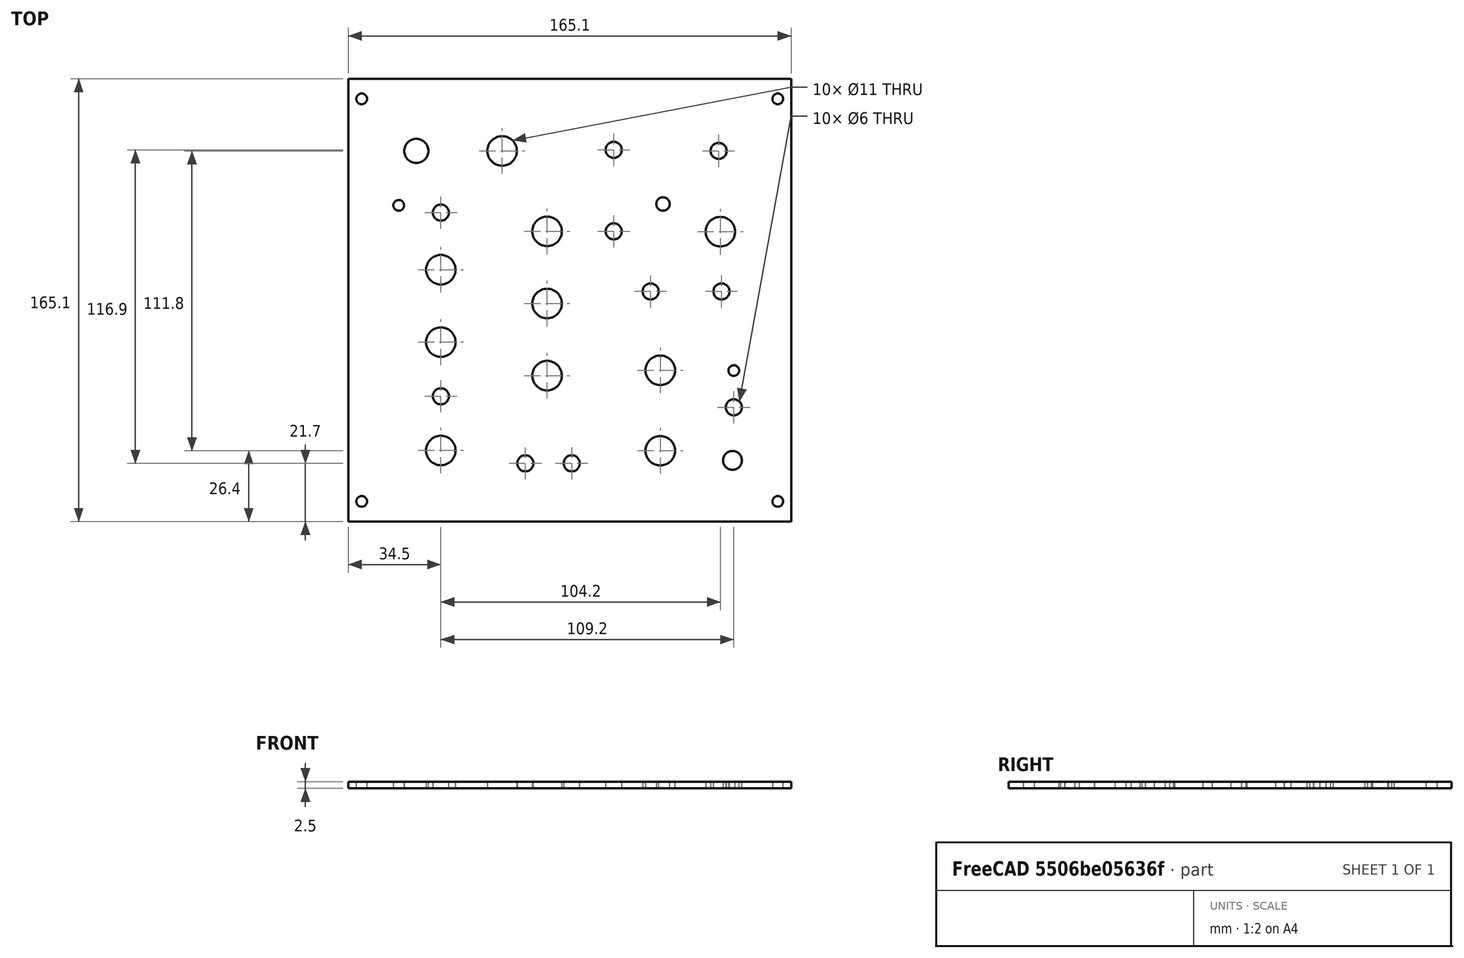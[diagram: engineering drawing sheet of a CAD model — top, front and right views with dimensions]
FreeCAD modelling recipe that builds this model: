
FCSTD DOCUMENT  (FreeCAD 0.21R33771 (Git))
Label: Front_Panel
License: All rights reserved
LicenseURL: http://en.wikipedia.org/wiki/All_rights_reserved
objects: Sketcher::SketchObject×1, PartDesign::Pad×1, PartDesign::CoordinateSystem×1, PartDesign::Body×1
note: 5 computed .brp shape members not serialized (recipe doc carries the construction recipe); baked Part::Feature solids carry a one-line shape summary decoded from their .brp
EXTERNAL_REF file=Noise_Toaster_Classic.FCStd obj=Spreadsheet

FEATURE [Sketcher::SketchObject] Sketch  label="dimensions"
  FullyConstrained = true
  Support = -> [XY_Plane]
  expr: Constraints[9] = Noise_Toaster_Classic#<<measurements>>.Front_width
  sketch-geometry (33):
    g0: LineSegment StartX=0 StartY=0 StartZ=0 EndX=165.1 EndY=0 EndZ=0
    g1: LineSegment StartX=165.1 StartY=0 StartZ=0 EndX=165.1 EndY=165.1 EndZ=0
    g2: LineSegment StartX=165.1 StartY=165.1 StartZ=0 EndX=0 EndY=165.1 EndZ=0
    g3: LineSegment StartX=0 StartY=165.1 StartZ=0 EndX=0 EndY=0 EndZ=0
    g4: Circle CenterX=5 CenterY=157.6 CenterZ=0 NormalX=0 NormalY=0 NormalZ=1 AngleXU=0 Radius=2
    g5: Circle CenterX=5 CenterY=7.5 CenterZ=0 NormalX=0 NormalY=0 NormalZ=1 AngleXU=0 Radius=2
    g6: Circle CenterX=160.1 CenterY=7.5 CenterZ=0 NormalX=0 NormalY=0 NormalZ=1 AngleXU=0 Radius=2
    g7: Circle CenterX=160.1 CenterY=157.6 CenterZ=0 NormalX=0 NormalY=0 NormalZ=1 AngleXU=0 Radius=2
    g8: Circle CenterX=34.5 CenterY=26.5 CenterZ=0 NormalX=0 NormalY=0 NormalZ=1 AngleXU=0 Radius=5.5
    g9: Circle CenterX=34.5 CenterY=46.7 CenterZ=0 NormalX=0 NormalY=0 NormalZ=1 AngleXU=0 Radius=3
    g10: Circle CenterX=34.5 CenterY=66.9 CenterZ=0 NormalX=0 NormalY=0 NormalZ=1 AngleXU=0 Radius=5.5
    g11: Circle CenterX=34.5 CenterY=93.9 CenterZ=0 NormalX=0 NormalY=0 NormalZ=1 AngleXU=0 Radius=5.5
    g12: Circle CenterX=34.5 CenterY=115.2 CenterZ=0 NormalX=0 NormalY=0 NormalZ=1 AngleXU=0 Radius=3
    g13: Circle CenterX=18.8 CenterY=117.9 CenterZ=0 NormalX=0 NormalY=0 NormalZ=1 AngleXU=0 Radius=2
    g14: Circle CenterX=25.35 CenterY=138.2 CenterZ=0 NormalX=0 NormalY=0 NormalZ=1 AngleXU=0 Radius=4.5
    g15: Circle CenterX=57.35 CenterY=138.2 CenterZ=0 NormalX=0 NormalY=0 NormalZ=1 AngleXU=0 Radius=5.5
    g16: Circle CenterX=98.9481 CenterY=138.6 CenterZ=0 NormalX=0 NormalY=0 NormalZ=1 AngleXU=0 Radius=3
    g17: Circle CenterX=138.046 CenterY=138.2 CenterZ=0 NormalX=0 NormalY=0 NormalZ=1 AngleXU=0 Radius=3
    g18: Circle CenterX=66 CenterY=21.7 CenterZ=0 NormalX=0 NormalY=0 NormalZ=1 AngleXU=0 Radius=3
    g19: Circle CenterX=83.3 CenterY=21.7 CenterZ=0 NormalX=0 NormalY=0 NormalZ=1 AngleXU=0 Radius=3
    g20: Circle CenterX=74.1 CenterY=54.4 CenterZ=0 NormalX=0 NormalY=0 NormalZ=1 AngleXU=0 Radius=5.5
    g21: Circle CenterX=74.1 CenterY=81.3 CenterZ=0 NormalX=0 NormalY=0 NormalZ=1 AngleXU=0 Radius=5.5
    g22: Circle CenterX=74.1 CenterY=108.2 CenterZ=0 NormalX=0 NormalY=0 NormalZ=1 AngleXU=0 Radius=5.5
    g23: Circle CenterX=98.9481 CenterY=108.2 CenterZ=0 NormalX=0 NormalY=0 NormalZ=1 AngleXU=0 Radius=3
    g24: Circle CenterX=116.3 CenterY=26.4 CenterZ=0 NormalX=0 NormalY=0 NormalZ=1 AngleXU=0 Radius=5.5
    g25: Circle CenterX=116.3 CenterY=56.4 CenterZ=0 NormalX=0 NormalY=0 NormalZ=1 AngleXU=0 Radius=5.5
    g26: Circle CenterX=143.2 CenterY=22.8 CenterZ=0 NormalX=0 NormalY=0 NormalZ=1 AngleXU=0 Radius=3.5
    g27: Circle CenterX=143.7 CenterY=42.5937 CenterZ=0 NormalX=0 NormalY=0 NormalZ=1 AngleXU=0 Radius=3
    g28: Circle CenterX=143.7 CenterY=56.2937 CenterZ=0 NormalX=0 NormalY=0 NormalZ=1 AngleXU=0 Radius=2
    g29: Circle CenterX=139.1 CenterY=85.8 CenterZ=0 NormalX=0 NormalY=0 NormalZ=1 AngleXU=0 Radius=3
    g30: Circle CenterX=138.7 CenterY=108.096 CenterZ=0 NormalX=0 NormalY=0 NormalZ=1 AngleXU=0 Radius=5.5
    g31: Circle CenterX=112.7 CenterY=85.8 CenterZ=0 NormalX=0 NormalY=0 NormalZ=1 AngleXU=0 Radius=3
    g32: Circle CenterX=117.3 CenterY=118.4 CenterZ=0 NormalX=0 NormalY=0 NormalZ=1 AngleXU=0 Radius=2.5
  constraints (98):
    c: Coincident(g0,g1)
    c: Coincident(g1,g2)
    c: Coincident(g2,g3)
    c: Coincident(g3,g0)
    c: Horizontal(g0)
    c: Horizontal(g2)
    c: Vertical(g1)
    c: Vertical(g3)
    c: Coincident(g0,g-1)
    c: DistanceX(g0,g0) = 165.1
    c: Equal(g0,g3)
    c: Distance(g4,g2) = 7.5
    c: Distance(g4,g3) = 5
    c: Radius(g4) = 2
    c: Equal(g4,g7)
    c: Equal(g5,g6)
    c: Equal(g4,g5)
    c: Distance(g7,g1) = 5
    c: Distance(g7,g2) = 7.5
    c: Distance(g5,g3) = 5
    c: Distance(g5,g0) = 7.5
    c: Distance(g6,g1) = 5
    c: Distance(g6,g0) = 7.5
    c: Distance(g8,g0) = 26.5
    c: Distance(g8,g3) = 34.5
    c: Radius(g8) = 5.5
    c: Distance(g8,g9) = 20.2
    c: Vertical(g9,g8)
    c: Radius(g9) = 3
    c: Distance(g9,g10) = 20.2
    c: Vertical(g10,g9)
    c: Radius(g10) = 5.5
    c: Vertical(g11,g10)
    c: Distance(g11,g10) = 27
    c: Radius(g11) = 5.5
    c: Vertical(g12,g11)
    c: Radius(g12) = 3
    c: Distance(g12,g11) = 21.3
    c: Distance(g13,g2) = 47.2
    c: Distance(g13,g3) = 18.8
    c: Radius(g13) = 2
    c: Distance(g14,g2) = 26.9
    c: Radius(g14) = 4.5
    c: Distance(g14,g3) = 25.35
    c: Horizontal(g15,g14)
    c: Horizontal(g17,g15)
    c: Radius(g16) = 3
    c: Radius(g17) = 3
    c: Radius(g15) = 5.5
    c: Distance(g14,g15) = 32
    c: Distance(g16,g15) = 41.6
    c: Distance(g16,g17) = 39.1
    c: Distance(g16,g2) = 23.5
    c: Radius(g18) = 3
    c: Radius(g19) = 3
    c: Horizontal(g19,g18)
    c: Distance(g18,g19) = 17.3
    c: DistanceY(g0,g18) = 21.7
    c: Distance(g18,g3) = 66
    c: Radius(g20) = 5.5
    c: Radius(g21) = 5.5
    c: Radius(g22) = 5.5
    c: Vertical(g22,g21)
    c: Vertical(g21,g20)
    c: Distance(g20,g3) = 74.1
    c: Distance(g20,g21) = 26.9
    c: Distance(g21,g22) = 26.9
    c: Distance(g20,g0) = 54.4
    c: Radius(g23) = 3
    c: Vertical(g16,g23)
    c: Horizontal(g23,g22)
    c: Vertical(g24,g25)
    c: Distance(g24,g0) = 26.4
    c: Distance(g24,g25) = 30
    c: Radius(g24) = 5.5
    c: Radius(g25) = 5.5
    c: Distance(g26,g1) = 21.9
    c: Distance(g27,g1) = 21.4
    c: Vertical(g27,g28)
    c: Distance(g28,g27) = 13.7
    c: Radius(g28) = 2
    c: Radius(g27) = 3
    c: Distance(g27,g26) = 19.8
    c: Distance(g26,g0) = 22.8
    c: Radius(g26) = 3.5
    c: Distance(g24,g1) = 48.8
    c: Distance(g29,g1) = 26
    c: Distance(g30,g1) = 26.4
    c: Distance(g30,g29) = 22.3
    c: Radius(g30) = 5.5
    c: Radius(g29) = 3
    c: Distance(g29,g0) = 85.8
    c: Horizontal(g29,g31)
    c: Radius(g31) = 3
    c: Distance(g29,g31) = 26.4
    c: Distance(g32,g1) = 47.8
    c: Radius(g32) = 2.5
    c: Distance(g32,g2) = 46.7
FEATURE [PartDesign::Pad] Pad
  Direction = (0,0,1)
  Length = 2.5
  Length2 = 10
  Profile = -> Sketch
  ReferenceAxis = -> Sketch [N_Axis]
  Type = 0
  expr: Length = Noise_Toaster_Classic#<<measurements>>.Front_thickness
FEATURE [PartDesign::CoordinateSystem] Front_LCS001  label="Front_LCS"
  AttacherType = Attacher::AttachEngine3D
  Support = -> [Pad,Origin]
FEATURE [PartDesign::Body] Body  label="Körper"
  Group = -> [Sketch,Pad,Front_LCS001]
  Origin = -> Origin
  Tip = -> Pad
